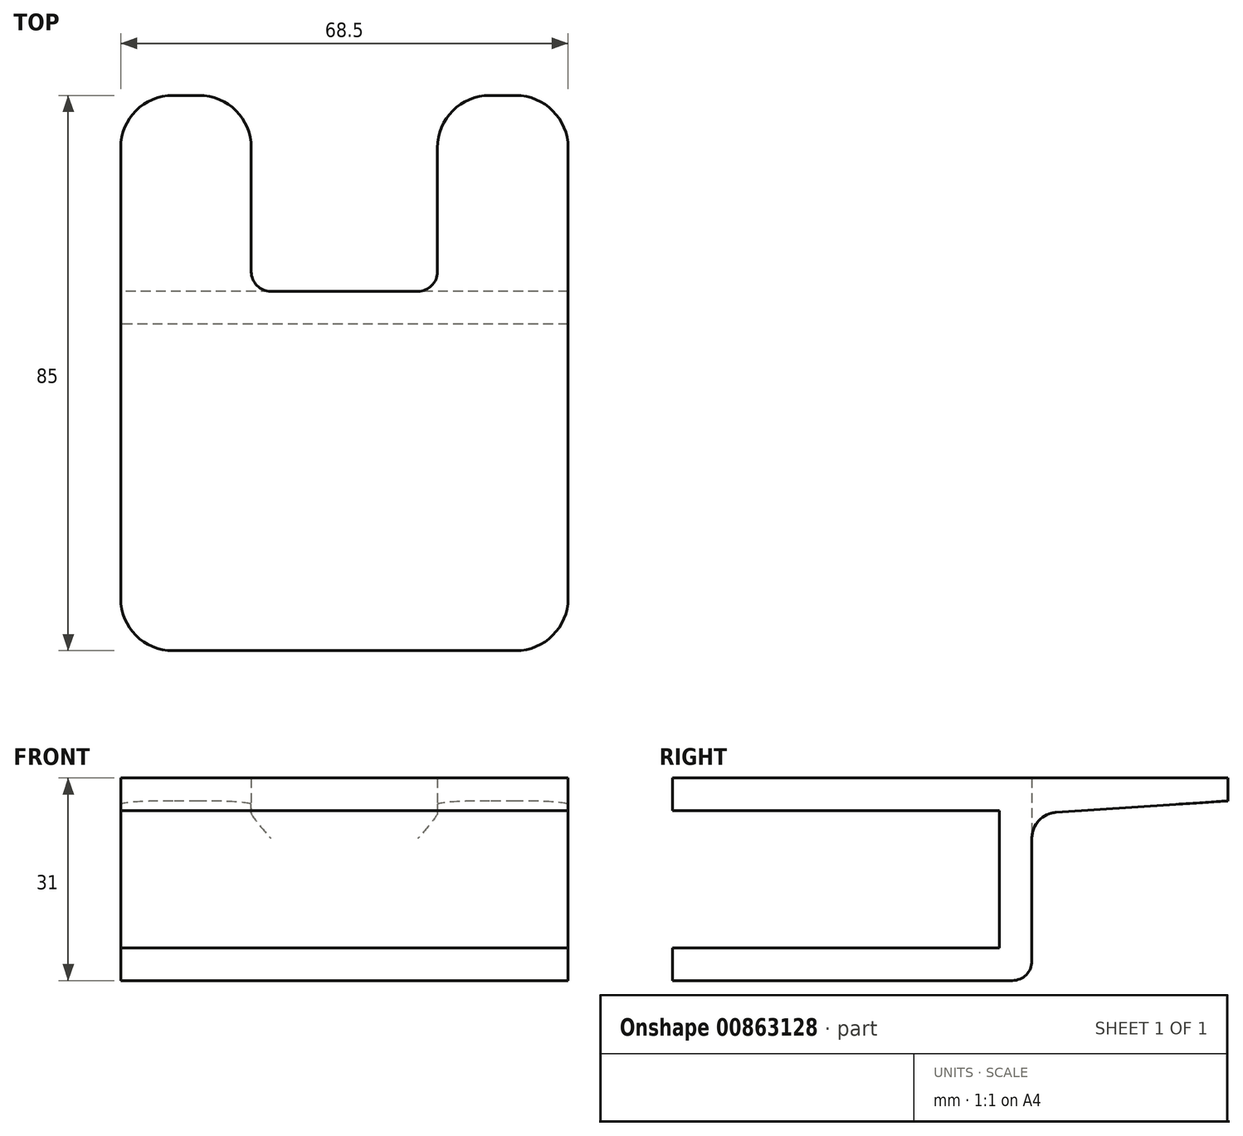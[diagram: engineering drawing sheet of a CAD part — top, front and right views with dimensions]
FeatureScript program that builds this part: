
annotation { "Feature Type Name" : "Feature", "Feature Type Description" : "" }
export const myFeature = defineFeature(function(context is Context, id is Id, definition is map)
    precondition{}
    {
        {
            var Q0;
            Q0=qCreatedBy(makeId("Top.planeOp"),FACE);
            var sketch = newSketch(context, id + "F0", { "sketchPlane" : qUnion([Q0])});
            skLineSegment(sketch, "E0", {"start": v(-34.25, 22) * mm, "end": v(-34.25, -47) * mm});
            skLineSegment(sketch, "E1", {"start": v(-26.25, -55) * mm, "end": v(26.25, -55) * mm});
            skLineSegment(sketch, "E2", {"start": v(34.25, -47) * mm, "end": v(34.25, 22) * mm});
            skLineSegment(sketch, "E3", {"start": v(26.25, 30) * mm, "end": v(22.25, 30) * mm});
            skLineSegment(sketch, "E4", {"start": v(14.25, 22) * mm, "end": v(14.25, 3) * mm});
            skLineSegment(sketch, "E5", {"start": v(11.25, 0) * mm, "end": v(-11.25, 0) * mm});
            skLineSegment(sketch, "E6", {"start": v(-14.25, 3) * mm, "end": v(-14.25, 22) * mm});
            skLineSegment(sketch, "E7", {"start": v(-22.25, 30) * mm, "end": v(-26.25, 30) * mm});
            skPoint(sketch, "E8.visualSharp", {"position": v(-34.25, -55) * mm});
            skArc(sketch, "E8.filletArc", {"start": v(-34.25, -47) * mm, "mid": v(-31.9, -52.66) * mm, "end": v(-26.25, -55) * mm});
            skPoint(sketch, "E9.visualSharp", {"position": v(34.25, -55) * mm});
            skArc(sketch, "E9.filletArc", {"start": v(26.25, -55) * mm, "mid": v(31.9, -52.66) * mm, "end": v(34.25, -47) * mm});
            skPoint(sketch, "E10.visualSharp", {"position": v(-34.25, 30) * mm});
            skArc(sketch, "E10.filletArc", {"start": v(-26.25, 30) * mm, "mid": v(-31.9, 27.66) * mm, "end": v(-34.25, 22) * mm});
            skPoint(sketch, "E11.visualSharp", {"position": v(-14.25, 30) * mm});
            skArc(sketch, "E11.filletArc", {"start": v(-14.25, 22) * mm, "mid": v(-16.6, 27.66) * mm, "end": v(-22.25, 30) * mm});
            skPoint(sketch, "E12.visualSharp", {"position": v(14.25, 30) * mm});
            skArc(sketch, "E12.filletArc", {"start": v(22.25, 30) * mm, "mid": v(16.6, 27.66) * mm, "end": v(14.25, 22) * mm});
            skPoint(sketch, "E13.visualSharp", {"position": v(34.25, 30) * mm});
            skArc(sketch, "E13.filletArc", {"start": v(34.25, 22) * mm, "mid": v(31.9, 27.66) * mm, "end": v(26.25, 30) * mm});
            skPoint(sketch, "E14.visualSharp", {"position": v(-14.25, 0) * mm});
            skArc(sketch, "E14.filletArc", {"start": v(-14.25, 3) * mm, "mid": v(-13.37, 0.88) * mm, "end": v(-11.25, 0) * mm});
            skPoint(sketch, "E15.visualSharp", {"position": v(14.25, 0) * mm});
            skArc(sketch, "E15.filletArc", {"start": v(11.25, 0) * mm, "mid": v(13.37, 0.88) * mm, "end": v(14.25, 3) * mm});
            skSolve(sketch);
        }
        {
            var Q0;
            Q0 = qSketchRegion(id + "F0", true);
            extrude(context, id + "F1", {"entities" : qUnion([Q0]), "depth" : 5.5 * mm, "offsetDistance" : 25 * mm});
        }
        {
            var Q0;
            Q0=makeQuery(id+"F1.opExtrude","SWEPT_FACE",FACE,{"disambiguationData":[OSD([sQuery(id+"F0.wireOp",EDGE,"E0")])]});
            var sketch = newSketch(context, id + "F2", { "sketchPlane" : qUnion([Q0])});
            skLineSegment(sketch, "E16", {"start": v(55, -3) * mm, "end": v(-30, -3) * mm});
            skLineSegment(sketch, "E17", {"start": v(-30, 2) * mm, "end": v(-30, -3) * mm});
            skLineSegment(sketch, "E18", {"start": v(0, 0.5) * mm, "end": v(55, 0.5) * mm});
            skLineSegment(sketch, "E19", {"start": v(55, -3) * mm, "end": v(55, 0.5) * mm});
            skLineSegment(sketch, "E20", {"start": v(0, 0) * mm, "end": v(-30, 2) * mm});
            skLineSegment(sketch, "E21", {"start": v(0, 0) * mm, "end": v(0, 0) * mm});
            skLineSegment(sketch, "E22", {"start": v(0, 0) * mm, "end": v(0, 0.5) * mm});
            skSolve(sketch);
        }
        {
            var Q0;
            Q0 = qSketchRegion(id + "F2", true);
            extrude(context, id + "F3", {"entities" : qUnion([Q0]), "operationType" : NewBodyOperationType.REMOVE, "endBound" : BoundingType.THROUGH_ALL, "oppositeDirection" : true, "depth" : 25 * mm, "offsetDistance" : 25 * mm});
        }
        {
            var Q0;
            Q0=makeQuery(id+"F3.boolean.opBoolean","COPY",FACE,{"derivedFrom":makeQuery(id+"F3.opExtrude","SWEPT_FACE",FACE,{"disambiguationData":[OSD([sQuery(id+"F2.wireOp",EDGE,"E18")])]})});
            var sketch = newSketch(context, id + "F4", { "sketchPlane" : qUnion([Q0])});
            skLineSegment(sketch, "E23.bottom", {"start": v(34.25, 0) * mm, "end": v(-34.25, 0) * mm});
            skLineSegment(sketch, "E23.top", {"start": v(34.25, 5) * mm, "end": v(-34.25, 5) * mm});
            skLineSegment(sketch, "E23.left", {"start": v(34.25, 0) * mm, "end": v(34.25, 5) * mm});
            skLineSegment(sketch, "E23.right", {"start": v(-34.25, 0) * mm, "end": v(-34.25, 5) * mm});
            skSolve(sketch);
        }
        {
            var Q0;
            Q0 = qSketchRegion(id + "F4", true);
            extrude(context, id + "F5", {"entities" : qUnion([Q0]), "operationType" : NewBodyOperationType.ADD, "depth" : 21 * mm, "offsetDistance" : 25 * mm});
        }
        {
            var Q0;
            {var subQ0=sQuery(id+"F0.wireOp",EDGE,"E0");var subQ1=sQuery(id+"F2.wireOp",EDGE,"E22");var subQ2=sQuery(id+"F2.wireOp",EDGE,"E20");Q0=makeQuery(id+"F3.boolean.opBoolean","COPY",EDGE,{"disambiguationData":[TD([makeQuery(id+"F1.opExtrude","SWEPT_FACE",FACE,{"disambiguationData":[OSD([subQ0])]})])],"derivedFrom":makeQuery(id+"F3.opExtrude","SWEPT_EDGE",EDGE,{"disambiguationData":[OSD([subQ0,subQ2,subQ1])]})});}
            var Q1;
            {var subQ0=sQuery(id+"F2.wireOp",EDGE,"E20");var subQ1=sQuery(id+"F2.wireOp",EDGE,"E22");Q1=makeQuery(id+"F3.boolean.opBoolean","COPY",EDGE,{"disambiguationData":[TD([makeQuery(id+"F1.opExtrude","SWEPT_FACE",FACE,{"disambiguationData":[OSD([sQuery(id+"F0.wireOp",EDGE,"E2")])]})])],"derivedFrom":makeQuery(id+"F3.opExtrude","SWEPT_EDGE",EDGE,{"disambiguationData":[OSD([sQuery(id+"F0.wireOp",EDGE,"E0"),subQ0,subQ1])]})});}
            fillet(context, id + "F6", {"entities" : qUnion([Q0, Q1]), "radius" : 4 * mm, "tangentPropagation" : true, "allowEdgeOverflow" : false});
        }
        {
            var Q0;
            Q0=makeQuery(id+"F5.opExtrude","CAP_FACE",FACE,{"disambiguationData":[OSD([sQuery(id+"F4.wireOp",EDGE,"E23.bottom"),sQuery(id+"F4.wireOp",EDGE,"E23.top"),sQuery(id+"F4.wireOp",EDGE,"E23.left"),sQuery(id+"F4.wireOp",EDGE,"E23.right")])],"isStart":false});
            var sketch = newSketch(context, id + "F7", { "sketchPlane" : qUnion([Q0])});
            skLineSegment(sketch, "E24", {"start": v(34.25, 0) * mm, "end": v(-34.25, 0) * mm});
            skLineSegment(sketch, "E25", {"start": v(-34.25, 0) * mm, "end": v(-34.25, 47) * mm});
            skLineSegment(sketch, "E26", {"start": v(-26.25, 55) * mm, "end": v(26.25, 55) * mm});
            skLineSegment(sketch, "E27", {"start": v(34.25, 47) * mm, "end": v(34.25, 0) * mm});
            skPoint(sketch, "E28.visualSharp", {"position": v(-34.25, 55) * mm});
            skArc(sketch, "E28.filletArc", {"start": v(-26.25, 55) * mm, "mid": v(-31.9, 52.66) * mm, "end": v(-34.25, 47) * mm});
            skPoint(sketch, "E29.visualSharp", {"position": v(34.25, 55) * mm});
            skArc(sketch, "E29.filletArc", {"start": v(34.25, 47) * mm, "mid": v(31.9, 52.66) * mm, "end": v(26.25, 55) * mm});
            skSolve(sketch);
        }
        {
            var Q0;
            Q0 = qSketchRegion(id + "F7", true);
            extrude(context, id + "F8", {"entities" : qUnion([Q0]), "operationType" : NewBodyOperationType.ADD, "depth" : 5 * mm, "offsetDistance" : 25 * mm});
        }
        {
            var Q0;
            Q0=makeQuery(id+"F8.opExtrude","CAP_EDGE",EDGE,{"disambiguationData":[OSD([sQuery(id+"F7.wireOp",EDGE,"E24")])],"isStart":false});
            var Q1;
            Q1=makeQuery(id+"F5.opExtrude","CAP_EDGE",EDGE,{"disambiguationData":[OSD([sQuery(id+"F4.wireOp",EDGE,"E23.top")])],"isStart":false});
            var Q2;
            Q2=makeQuery(id+"F5.opExtrude","CAP_EDGE",EDGE,{"disambiguationData":[OSD([sQuery(id+"F4.wireOp",EDGE,"E23.top")])],"isStart":true});
            fillet(context, id + "F9", {"entities" : qUnion([Q0, Q1, Q2]), "radius" : 3 * mm, "tangentPropagation" : true, "allowEdgeOverflow" : false});
        }
    });
